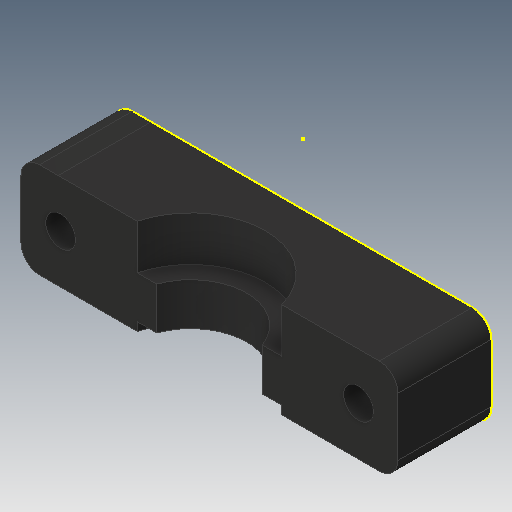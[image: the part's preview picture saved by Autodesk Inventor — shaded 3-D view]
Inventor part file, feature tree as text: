
AUTODESK INVENTOR PART (.ipt)
format: ipt  version: 2017 (Build 210142000, 142)  size: 162,816 bytes
history: native  units: in
note: dims shown in document units (in); Inventor stores cm internally (conversion verified against a paired STEP export)
features: sketch x5, extrude x4, other x3, reference x1, projected_geometry x1
ambient origin geometry x8: Origin, YZ Plane, XZ Plane, XY Plane, X Axis, Y Axis, Z Axis, Center Point
bodies: Solid1 (feature_tree)
feature tree (14):
  extrude  "Extrusion1"  Depth=0.0787in
  extrude  "Extrusion2"  Depth=0.0787in
  extrude  "Extrusion3"  Depth=0.189in TaperAngle=0.0deg
  extrude  "Extrusion4"  Depth=0.189in TaperAngle=0.0deg
  sketch  "Sketch5"  dims[d12=0.6299in d13=0.0354in d14=0.0in]
  sketch  "Sketch1"  dims[d1=0.0787in d2=0.0787in]
  reference  "Reference1"
  sketch  "Sketch2"  dims[d3=0.3937in d4=0.0in d5=0.0787in]
  sketch  "Sketch3"  dims[d6=0.6299in d7=0.189in d8=0.0in]
  sketch  "Sketch4"  dims[d9=0.4724in d10=0.189in d11=0.0in]
  projected_geometry  "Projected Loop1"
  other  "<userpath>\OneDrive\Inventor\Beast 3D Printer\Hotend Mount Assembly.iam"
  other  "Hotend Mount Assembly.iam"
  other  "Hotend Slide Part 1:1"
